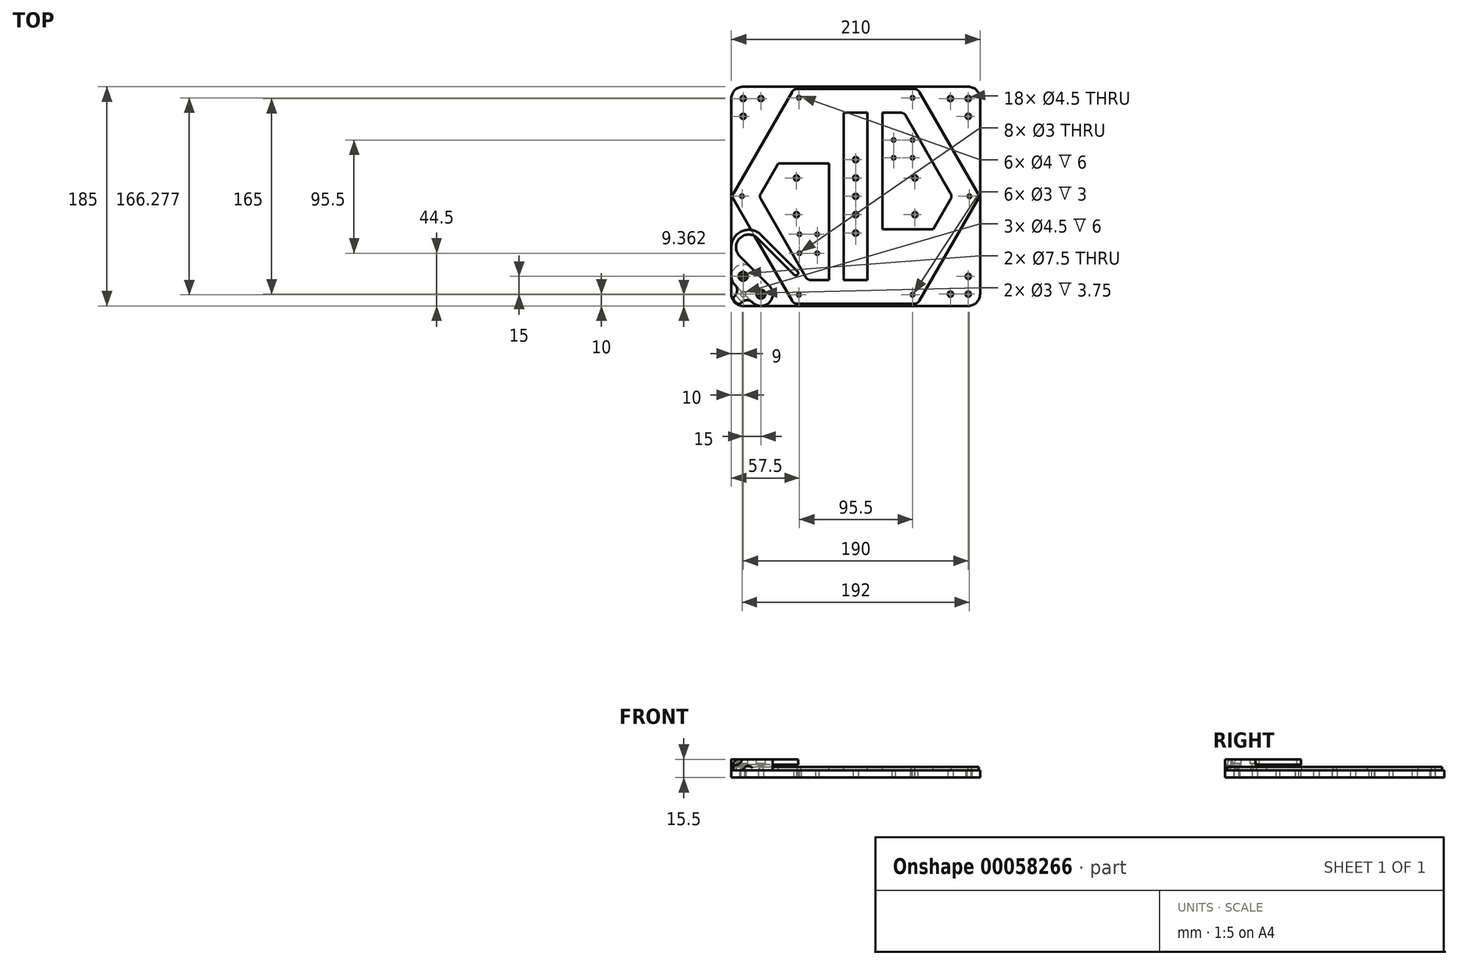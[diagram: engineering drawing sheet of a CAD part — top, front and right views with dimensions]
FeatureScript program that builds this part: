
annotation { "Feature Type Name" : "Feature", "Feature Type Description" : "" }
export const myFeature = defineFeature(function(context is Context, id is Id, definition is map)
    precondition{}
    {
        {
            var Q0;
            Q0=qCreatedBy(makeId("Top.planeOp"),FACE);
            var sketch = newSketch(context, id + "F0", { "sketchPlane" : qUnion([Q0])});
            skLineSegment(sketch, "E0.bottom", {"start": v(105, 92.5) * mm, "end": v(-105, 92.5) * mm});
            skLineSegment(sketch, "E0.top", {"start": v(105, -92.5) * mm, "end": v(-105, -92.5) * mm});
            skLineSegment(sketch, "E0.left", {"start": v(105, 92.5) * mm, "end": v(105, -92.5) * mm});
            skLineSegment(sketch, "E0.right", {"start": v(-105, 92.5) * mm, "end": v(-105, -92.5) * mm});
            skPoint(sketch, "E0.middle", {"position": v(0, 0) * mm});
            skCircle(sketch, "E1", {"center": v(0, 0) * mm, "radius": 96 * mm, "construction": true});
            skLineSegment(sketch, "E2", {"start": v(0, 0) * mm, "end": v(-96, 0) * mm, "construction": true});
            skCircle(sketch, "E3", {"center": v(-96, 0) * mm, "radius": 2 * mm});
            skCircle(sketch, "E4.1.0", {"center": v(-48, -83.14) * mm, "radius": 2 * mm});
            skCircle(sketch, "E4.2.0", {"center": v(48, -83.14) * mm, "radius": 2 * mm});
            skCircle(sketch, "E4.3.0", {"center": v(96, 0) * mm, "radius": 2 * mm});
            skCircle(sketch, "E4.4.0", {"center": v(48, 83.14) * mm, "radius": 2 * mm});
            skCircle(sketch, "E4.5.0", {"center": v(-48, 83.14) * mm, "radius": 2 * mm});
            skSolve(sketch);
        }
        {
            var Q0;
            Q0 = qSketchRegion(id + "F0", true);
            extrude(context, id + "F1", {"entities" : qUnion([Q0]), "depth" : 6 * mm});
        }
        {
            var Q0;
            Q0=makeQuery(id+"F1.opExtrude","SWEPT_EDGE",EDGE,{"disambiguationData":[OSD([sQuery(id+"F0.wireOp",EDGE,"E0.top"),sQuery(id+"F0.wireOp",EDGE,"E0.right")])]});
            var Q1;
            Q1=makeQuery(id+"F1.opExtrude","SWEPT_EDGE",EDGE,{"disambiguationData":[OSD([sQuery(id+"F0.wireOp",EDGE,"E0.top"),sQuery(id+"F0.wireOp",EDGE,"E0.left")])]});
            var Q2;
            Q2=makeQuery(id+"F1.opExtrude","SWEPT_EDGE",EDGE,{"disambiguationData":[OSD([sQuery(id+"F0.wireOp",EDGE,"E0.bottom"),sQuery(id+"F0.wireOp",EDGE,"E0.right")])]});
            var Q3;
            Q3=makeQuery(id+"F1.opExtrude","SWEPT_EDGE",EDGE,{"disambiguationData":[OSD([sQuery(id+"F0.wireOp",EDGE,"E0.bottom"),sQuery(id+"F0.wireOp",EDGE,"E0.left")])]});
            fillet(context, id + "F2", {"entities" : qUnion([Q0, Q1, Q2, Q3]), "radius" : 10 * mm, "tangentPropagation" : true, "allowEdgeOverflow" : false});
        }
        {
            var Q0;
            Q0=makeQuery(id+"F1.opExtrude","CAP_FACE",FACE,{"disambiguationData":[OSD([sQuery(id+"F0.wireOp",EDGE,"E0.bottom"),sQuery(id+"F0.wireOp",EDGE,"E0.top"),sQuery(id+"F0.wireOp",EDGE,"E0.left"),sQuery(id+"F0.wireOp",EDGE,"E0.right"),sQuery(id+"F0.wireOp",EDGE,"E3"),sQuery(id+"F0.wireOp",EDGE,"E4.1.0"),sQuery(id+"F0.wireOp",EDGE,"E4.2.0"),sQuery(id+"F0.wireOp",EDGE,"E4.3.0"),sQuery(id+"F0.wireOp",EDGE,"E4.4.0"),sQuery(id+"F0.wireOp",EDGE,"E4.5.0")])],"isStart":true});
            var sketch = newSketch(context, id + "F3", { "sketchPlane" : qUnion([Q0])});
            skLineSegment(sketch, "E5", {"start": v(0, 0) * mm, "end": v(-105, 0) * mm, "construction": true});
            skCircle(sketch, "E6", {"center": v(0, 0) * mm, "radius": 96 * mm, "construction": true});
            skPoint(sketch, "E7", {"position": v(-96, 0) * mm});
            skLineSegment(sketch, "E8.bottom", {"start": v(40, 40) * mm, "end": v(-40, 40) * mm, "construction": true});
            skLineSegment(sketch, "E8.top", {"start": v(40, -40) * mm, "end": v(-40, -40) * mm, "construction": true});
            skLineSegment(sketch, "E8.left", {"start": v(40, 40) * mm, "end": v(40, -40) * mm, "construction": true});
            skLineSegment(sketch, "E8.right", {"start": v(-40, 40) * mm, "end": v(-40, -40) * mm, "construction": true});
            skLineSegment(sketch, "E9.bottom", {"start": v(-32.5, 48) * mm, "end": v(-47.5, 48) * mm, "construction": true});
            skLineSegment(sketch, "E9.top", {"start": v(-32.5, 32) * mm, "end": v(-47.5, 32) * mm, "construction": true});
            skLineSegment(sketch, "E9.left", {"start": v(-32.5, 48) * mm, "end": v(-32.5, 32) * mm, "construction": true});
            skLineSegment(sketch, "E9.right", {"start": v(-47.5, 48) * mm, "end": v(-47.5, 32) * mm, "construction": true});
            skPoint(sketch, "E9.middle", {"position": v(-40, 40) * mm});
            skCircle(sketch, "E10", {"center": v(-47.5, 48) * mm, "radius": 1.5 * mm});
            skCircle(sketch, "E11", {"center": v(-32.5, 48) * mm, "radius": 1.5 * mm});
            skCircle(sketch, "E12", {"center": v(-47.5, 32) * mm, "radius": 1.5 * mm});
            skCircle(sketch, "E13", {"center": v(-32.5, 32) * mm, "radius": 1.5 * mm});
            skLineSegment(sketch, "E14", {"start": v(0, 0) * mm, "end": v(40, 40) * mm, "construction": true});
            skCircle(sketch, "E15.MirrorC", {"center": v(32, -47.5) * mm, "radius": 1.5 * mm});
            skCircle(sketch, "E16.MirrorC", {"center": v(32, -32.5) * mm, "radius": 1.5 * mm});
            skCircle(sketch, "E17.MirrorC", {"center": v(48, -32.5) * mm, "radius": 1.5 * mm});
            skCircle(sketch, "E18.MirrorC", {"center": v(48, -47.5) * mm, "radius": 1.5 * mm});
            skSolve(sketch);
        }
        {
            var Q0;
            Q0 = qSketchRegion(id + "F3", true);
            extrude(context, id + "F4", {"entities" : qUnion([Q0]), "operationType" : NewBodyOperationType.REMOVE, "endBound" : BoundingType.THROUGH_ALL, "oppositeDirection" : true, "depth" : 25 * mm});
        }
        {
            var Q0;
            Q0=makeQuery(id+"F1.opExtrude","CAP_FACE",FACE,{"disambiguationData":[OSD([sQuery(id+"F0.wireOp",EDGE,"E0.bottom"),sQuery(id+"F0.wireOp",EDGE,"E0.top"),sQuery(id+"F0.wireOp",EDGE,"E0.left"),sQuery(id+"F0.wireOp",EDGE,"E0.right"),sQuery(id+"F0.wireOp",EDGE,"E3"),sQuery(id+"F0.wireOp",EDGE,"E4.1.0"),sQuery(id+"F0.wireOp",EDGE,"E4.2.0"),sQuery(id+"F0.wireOp",EDGE,"E4.3.0"),sQuery(id+"F0.wireOp",EDGE,"E4.4.0"),sQuery(id+"F0.wireOp",EDGE,"E4.5.0")])],"isStart":true});
            var sketch = newSketch(context, id + "F5", { "sketchPlane" : qUnion([Q0])});
            skLineSegment(sketch, "E19", {"start": v(-47.5, 48) * mm, "end": v(-32.5, 32) * mm, "construction": true});
            skLineSegment(sketch, "E20", {"start": v(32, -32.5) * mm, "end": v(48, -47.5) * mm, "construction": true});
            skPoint(sketch, "E21", {"position": v(40, -40) * mm});
            skPoint(sketch, "E22", {"position": v(-40, 40) * mm});
            skLineSegment(sketch, "E23", {"start": v(40, -40) * mm, "end": v(40, -15.5) * mm, "construction": true});
            skLineSegment(sketch, "E24", {"start": v(40, -15.5) * mm, "end": v(0, -15.5) * mm, "construction": true});
            skLineSegment(sketch, "E25", {"start": v(0, -15.5) * mm, "end": v(0, 0) * mm, "construction": true});
            skLineSegment(sketch, "E26.bottom", {"start": v(15.5, 0) * mm, "end": v(-15.5, 0) * mm, "construction": true});
            skLineSegment(sketch, "E26.top", {"start": v(15.5, -31) * mm, "end": v(-15.5, -31) * mm, "construction": true});
            skLineSegment(sketch, "E26.left", {"start": v(15.5, 0) * mm, "end": v(15.5, -31) * mm, "construction": true});
            skLineSegment(sketch, "E26.right", {"start": v(-15.5, 0) * mm, "end": v(-15.5, -31) * mm, "construction": true});
            skPoint(sketch, "E26.middle", {"position": v(0, -15.5) * mm});
            skCircle(sketch, "E27", {"center": v(0, -31) * mm, "radius": 2.25 * mm});
            skCircle(sketch, "E28", {"center": v(0, 0) * mm, "radius": 2.25 * mm});
            skCircle(sketch, "E29.MirrorC", {"center": v(0, 31) * mm, "radius": 2.25 * mm});
            skCircle(sketch, "E30", {"center": v(0, -15.5) * mm, "radius": 2.25 * mm});
            skCircle(sketch, "E31.MirrorC", {"center": v(0, 15.5) * mm, "radius": 2.25 * mm});
            skSolve(sketch);
        }
        {
            var Q0;
            Q0 = qSketchRegion(id + "F5", true);
            extrude(context, id + "F6", {"entities" : qUnion([Q0]), "operationType" : NewBodyOperationType.REMOVE, "endBound" : BoundingType.THROUGH_ALL, "oppositeDirection" : true, "depth" : 25 * mm});
        }
        {
            var Q0;
            Q0=makeQuery(id+"F1.opExtrude","CAP_FACE",FACE,{"disambiguationData":[OSD([sQuery(id+"F0.wireOp",EDGE,"E0.bottom"),sQuery(id+"F0.wireOp",EDGE,"E0.top"),sQuery(id+"F0.wireOp",EDGE,"E0.left"),sQuery(id+"F0.wireOp",EDGE,"E0.right"),sQuery(id+"F0.wireOp",EDGE,"E3"),sQuery(id+"F0.wireOp",EDGE,"E4.1.0"),sQuery(id+"F0.wireOp",EDGE,"E4.2.0"),sQuery(id+"F0.wireOp",EDGE,"E4.3.0"),sQuery(id+"F0.wireOp",EDGE,"E4.4.0"),sQuery(id+"F0.wireOp",EDGE,"E4.5.0")])],"isStart":true});
            var sketch = newSketch(context, id + "F7", { "sketchPlane" : qUnion([Q0])});
            skLineSegment(sketch, "E32", {"start": v(0, 0) * mm, "end": v(49.14, 0) * mm, "construction": true});
            skLineSegment(sketch, "E33", {"start": v(0, 0) * mm, "end": v(0, -73.64) * mm, "construction": true});
            skLineSegment(sketch, "E34", {"start": v(0, 15.5) * mm, "end": v(50, 15.5) * mm, "construction": true});
            skCircle(sketch, "E35", {"center": v(50, 15.5) * mm, "radius": 2.25 * mm});
            skCircle(sketch, "E36.MirrorC", {"center": v(50, -15.5) * mm, "radius": 2.25 * mm});
            skCircle(sketch, "E37.MirrorC", {"center": v(-50, 15.5) * mm, "radius": 2.25 * mm});
            skCircle(sketch, "E38.MirrorC", {"center": v(-50, -15.5) * mm, "radius": 2.25 * mm});
            skSolve(sketch);
        }
        {
            var Q0;
            Q0 = qSketchRegion(id + "F7", true);
            extrude(context, id + "F8", {"entities" : qUnion([Q0]), "operationType" : NewBodyOperationType.REMOVE, "endBound" : BoundingType.THROUGH_ALL, "oppositeDirection" : true, "depth" : 25 * mm});
        }
        {
            var Q0;
            Q0=makeQuery(id+"F1.opExtrude","CAP_FACE",FACE,{"disambiguationData":[OSD([sQuery(id+"F0.wireOp",EDGE,"E0.bottom"),sQuery(id+"F0.wireOp",EDGE,"E0.top"),sQuery(id+"F0.wireOp",EDGE,"E0.left"),sQuery(id+"F0.wireOp",EDGE,"E0.right"),sQuery(id+"F0.wireOp",EDGE,"E3"),sQuery(id+"F0.wireOp",EDGE,"E4.1.0"),sQuery(id+"F0.wireOp",EDGE,"E4.2.0"),sQuery(id+"F0.wireOp",EDGE,"E4.3.0"),sQuery(id+"F0.wireOp",EDGE,"E4.4.0"),sQuery(id+"F0.wireOp",EDGE,"E4.5.0")])],"isStart":true});
            var sketch = newSketch(context, id + "F9", { "sketchPlane" : qUnion([Q0])});
            skCircle(sketch, "E39", {"center": v(0, 0) * mm, "radius": 96 * mm, "construction": true});
            skPoint(sketch, "E40", {"position": v(96, 0) * mm});
            skLineSegment(sketch, "E41", {"start": v(0, 0) * mm, "end": v(95, 82.5) * mm, "construction": true});
            skCircle(sketch, "E42", {"center": v(95, 82.5) * mm, "radius": 2.25 * mm});
            skLineSegment(sketch, "E43", {"start": v(95, 82.5) * mm, "end": v(95, 67.5) * mm, "construction": true});
            skCircle(sketch, "E44", {"center": v(95, 67.5) * mm, "radius": 2.25 * mm});
            skLineSegment(sketch, "E45", {"start": v(95, 82.5) * mm, "end": v(80, 82.5) * mm, "construction": true});
            skCircle(sketch, "E46", {"center": v(80, 82.5) * mm, "radius": 2.25 * mm});
            skLineSegment(sketch, "E47", {"start": v(0, 0) * mm, "end": v(0, 67.43) * mm, "construction": true});
            skLineSegment(sketch, "E48", {"start": v(0, 0) * mm, "end": v(-61.9, 0) * mm, "construction": true});
            skCircle(sketch, "E49.MirrorC", {"center": v(-95, 67.5) * mm, "radius": 2.25 * mm});
            skCircle(sketch, "E50.MirrorC", {"center": v(-95, 82.5) * mm, "radius": 2.25 * mm});
            skCircle(sketch, "E51.MirrorC", {"center": v(-80, 82.5) * mm, "radius": 2.25 * mm});
            skCircle(sketch, "E52.MirrorC", {"center": v(95, -67.5) * mm, "radius": 2.25 * mm});
            skCircle(sketch, "E53.MirrorC", {"center": v(95, -82.5) * mm, "radius": 2.25 * mm});
            skCircle(sketch, "E54.MirrorC", {"center": v(80, -82.5) * mm, "radius": 2.25 * mm});
            skCircle(sketch, "E55.MirrorC", {"center": v(-95, -67.5) * mm, "radius": 2.25 * mm});
            skCircle(sketch, "E56.MirrorC", {"center": v(-95, -82.5) * mm, "radius": 2.25 * mm});
            skCircle(sketch, "E57.MirrorC", {"center": v(-80, -82.5) * mm, "radius": 2.25 * mm});
            skSolve(sketch);
        }
        {
            var Q0;
            Q0 = qSketchRegion(id + "F9", true);
            extrude(context, id + "F10", {"entities" : qUnion([Q0]), "operationType" : NewBodyOperationType.REMOVE, "endBound" : BoundingType.THROUGH_ALL, "oppositeDirection" : true, "depth" : 25 * mm});
        }
        {
            var Q0;
            Q0=makeQuery(id+"F1.opExtrude","CAP_FACE",FACE,{"disambiguationData":[OSD([sQuery(id+"F0.wireOp",EDGE,"E0.bottom"),sQuery(id+"F0.wireOp",EDGE,"E0.top"),sQuery(id+"F0.wireOp",EDGE,"E0.left"),sQuery(id+"F0.wireOp",EDGE,"E0.right"),sQuery(id+"F0.wireOp",EDGE,"E3"),sQuery(id+"F0.wireOp",EDGE,"E4.1.0"),sQuery(id+"F0.wireOp",EDGE,"E4.2.0"),sQuery(id+"F0.wireOp",EDGE,"E4.3.0"),sQuery(id+"F0.wireOp",EDGE,"E4.4.0"),sQuery(id+"F0.wireOp",EDGE,"E4.5.0")])],"isStart":false});
            var sketch = newSketch(context, id + "F11", { "sketchPlane" : qUnion([Q0])});
            skLineSegment(sketch, "E58", {"start": v(-48, 83.14) * mm, "end": v(-96, 0) * mm, "construction": true});
            skLineSegment(sketch, "E59", {"start": v(-96, 0) * mm, "end": v(-48, -83.14) * mm, "construction": true});
            skLineSegment(sketch, "E60", {"start": v(-48, -83.14) * mm, "end": v(48, -83.14) * mm, "construction": true});
            skLineSegment(sketch, "E61", {"start": v(48, -83.14) * mm, "end": v(96, 0) * mm, "construction": true});
            skLineSegment(sketch, "E62", {"start": v(96, 0) * mm, "end": v(48, 83.14) * mm, "construction": true});
            skLineSegment(sketch, "E63", {"start": v(48, 83.14) * mm, "end": v(-48, 83.14) * mm, "construction": true});
            skLineSegment(sketch, "E64.0", {"start": v(104.66, 0) * mm, "end": v(52.33, 90.64) * mm});
            skLineSegment(sketch, "E64.1", {"start": v(-52.33, 90.64) * mm, "end": v(-104.66, 0) * mm});
            skLineSegment(sketch, "E64.2", {"start": v(-104.66, 0) * mm, "end": v(-52.33, -90.64) * mm});
            skLineSegment(sketch, "E64.3", {"start": v(52.33, 90.64) * mm, "end": v(-52.33, 90.64) * mm});
            skLineSegment(sketch, "E64.4", {"start": v(-52.33, -90.64) * mm, "end": v(52.33, -90.64) * mm});
            skLineSegment(sketch, "E64.5", {"start": v(52.33, -90.64) * mm, "end": v(104.66, 0) * mm});
            skLineSegment(sketch, "E65.0", {"start": v(81.57, 0) * mm, "end": v(40.78, 70.64) * mm});
            skLineSegment(sketch, "E65.1", {"start": v(-40.78, 70.64) * mm, "end": v(-81.57, 0) * mm});
            skLineSegment(sketch, "E65.2", {"start": v(-81.57, 0) * mm, "end": v(-40.78, -70.64) * mm});
            skLineSegment(sketch, "E65.3", {"start": v(40.78, 70.64) * mm, "end": v(-40.78, 70.64) * mm});
            skLineSegment(sketch, "E65.4", {"start": v(-40.78, -70.64) * mm, "end": v(40.78, -70.64) * mm});
            skLineSegment(sketch, "E65.5", {"start": v(40.78, -70.64) * mm, "end": v(81.57, 0) * mm});
            skCircle(sketch, "E66", {"center": v(-48, 83.14) * mm, "radius": 1.5 * mm});
            skCircle(sketch, "E67", {"center": v(48, 83.14) * mm, "radius": 1.5 * mm});
            skCircle(sketch, "E68", {"center": v(96, 0) * mm, "radius": 1.5 * mm});
            skCircle(sketch, "E69", {"center": v(48, -83.14) * mm, "radius": 1.5 * mm});
            skCircle(sketch, "E70", {"center": v(-48, -83.14) * mm, "radius": 1.5 * mm});
            skCircle(sketch, "E71", {"center": v(-96, 0) * mm, "radius": 1.5 * mm});
            skSolve(sketch);
        }
        {
            var Q0;
            Q0 = qSketchRegion(id + "F11", true);
            extrude(context, id + "F12", {"entities" : qUnion([Q0]), "depth" : 3 * mm});
        }
        {
            var Q0;
            Q0=makeQuery(id+"F12.opExtrude","CAP_FACE",FACE,{"disambiguationData":[OSD([sQuery(id+"F11.wireOp",EDGE,"E64.0"),sQuery(id+"F11.wireOp",EDGE,"E64.1"),sQuery(id+"F11.wireOp",EDGE,"E64.2"),sQuery(id+"F11.wireOp",EDGE,"E64.3"),sQuery(id+"F11.wireOp",EDGE,"E64.4"),sQuery(id+"F11.wireOp",EDGE,"E64.5"),sQuery(id+"F11.wireOp",EDGE,"E65.0"),sQuery(id+"F11.wireOp",EDGE,"E65.1"),sQuery(id+"F11.wireOp",EDGE,"E65.2"),sQuery(id+"F11.wireOp",EDGE,"E65.3"),sQuery(id+"F11.wireOp",EDGE,"E65.4"),sQuery(id+"F11.wireOp",EDGE,"E65.5"),sQuery(id+"F11.wireOp",EDGE,"E66"),sQuery(id+"F11.wireOp",EDGE,"E67"),sQuery(id+"F11.wireOp",EDGE,"E68"),sQuery(id+"F11.wireOp",EDGE,"E69"),sQuery(id+"F11.wireOp",EDGE,"E70"),sQuery(id+"F11.wireOp",EDGE,"E71")])],"isStart":false});
            var sketch = newSketch(context, id + "F13", { "sketchPlane" : qUnion([Q0])});
            skLineSegment(sketch, "E72", {"start": v(0, 70.64) * mm, "end": v(0, -70.64) * mm, "construction": true});
            skLineSegment(sketch, "E73.bottom", {"start": v(-10, 70.64) * mm, "end": v(-22.5, 70.64) * mm});
            skLineSegment(sketch, "E73.top", {"start": v(-10, -70.64) * mm, "end": v(-22.5, -70.64) * mm});
            skLineSegment(sketch, "E73.left", {"start": v(-10, 70.64) * mm, "end": v(-10, -70.64) * mm});
            skLineSegment(sketch, "E73.right", {"start": v(-22.5, 70.64) * mm, "end": v(-22.5, -70.64) * mm});
            skLineSegment(sketch, "E74.MirrorCS", {"start": v(22.5, 70.64) * mm, "end": v(22.5, -70.64) * mm});
            skLineSegment(sketch, "E75.MirrorCS", {"start": v(10, -70.64) * mm, "end": v(22.5, -70.64) * mm});
            skLineSegment(sketch, "E76.MirrorCS", {"start": v(10, 70.64) * mm, "end": v(10, -70.64) * mm});
            skLineSegment(sketch, "E77.MirrorCS", {"start": v(10, 70.64) * mm, "end": v(22.5, 70.64) * mm});
            skSolve(sketch);
        }
        {
            var Q0;
            Q0 = qSketchRegion(id + "F13", true);
            var Q1;
            Q1=makeQuery(id+"F12.opExtrude","CAP_FACE",FACE,{"disambiguationData":[OSD([sQuery(id+"F11.wireOp",EDGE,"E64.0"),sQuery(id+"F11.wireOp",EDGE,"E64.1"),sQuery(id+"F11.wireOp",EDGE,"E64.2"),sQuery(id+"F11.wireOp",EDGE,"E64.3"),sQuery(id+"F11.wireOp",EDGE,"E64.4"),sQuery(id+"F11.wireOp",EDGE,"E64.5"),sQuery(id+"F11.wireOp",EDGE,"E65.0"),sQuery(id+"F11.wireOp",EDGE,"E65.1"),sQuery(id+"F11.wireOp",EDGE,"E65.2"),sQuery(id+"F11.wireOp",EDGE,"E65.3"),sQuery(id+"F11.wireOp",EDGE,"E65.4"),sQuery(id+"F11.wireOp",EDGE,"E65.5"),sQuery(id+"F11.wireOp",EDGE,"E66"),sQuery(id+"F11.wireOp",EDGE,"E67"),sQuery(id+"F11.wireOp",EDGE,"E68"),sQuery(id+"F11.wireOp",EDGE,"E69"),sQuery(id+"F11.wireOp",EDGE,"E70"),sQuery(id+"F11.wireOp",EDGE,"E71")])],"isStart":true});
            extrude(context, id + "F14", {"entities" : qUnion([Q0]), "operationType" : NewBodyOperationType.ADD, "endBound" : BoundingType.UP_TO_SURFACE, "oppositeDirection" : true, "endBoundEntityFace" : qUnion([Q1]), "depth" : 25 * mm});
        }
        {
            var Q0;
            Q0=makeQuery(id+"F14.boolean.opBoolean","MERGE",FACE,{"derivedFrom":[makeQuery(id+"F12.opExtrude","CAP_FACE",FACE,{"disambiguationData":[OSD([sQuery(id+"F11.wireOp",EDGE,"E64.0"),sQuery(id+"F11.wireOp",EDGE,"E64.1"),sQuery(id+"F11.wireOp",EDGE,"E64.2"),sQuery(id+"F11.wireOp",EDGE,"E64.3"),sQuery(id+"F11.wireOp",EDGE,"E64.4"),sQuery(id+"F11.wireOp",EDGE,"E64.5"),sQuery(id+"F11.wireOp",EDGE,"E65.0"),sQuery(id+"F11.wireOp",EDGE,"E65.1"),sQuery(id+"F11.wireOp",EDGE,"E65.2"),sQuery(id+"F11.wireOp",EDGE,"E65.3"),sQuery(id+"F11.wireOp",EDGE,"E65.4"),sQuery(id+"F11.wireOp",EDGE,"E65.5"),sQuery(id+"F11.wireOp",EDGE,"E66"),sQuery(id+"F11.wireOp",EDGE,"E67"),sQuery(id+"F11.wireOp",EDGE,"E68"),sQuery(id+"F11.wireOp",EDGE,"E69"),sQuery(id+"F11.wireOp",EDGE,"E70"),sQuery(id+"F11.wireOp",EDGE,"E71")])],"isStart":false}),makeQuery(id+"F14.opExtrude","CAP_FACE",FACE,{"disambiguationData":[OSD([sQuery(id+"F13.wireOp",EDGE,"E73.bottom"),sQuery(id+"F13.wireOp",EDGE,"E73.top"),sQuery(id+"F13.wireOp",EDGE,"E73.left"),sQuery(id+"F13.wireOp",EDGE,"E73.right")])],"isStart":true}),makeQuery(id+"F14.opExtrude","CAP_FACE",FACE,{"disambiguationData":[OSD([sQuery(id+"F13.wireOp",EDGE,"E74.MirrorCS"),sQuery(id+"F13.wireOp",EDGE,"E75.MirrorCS"),sQuery(id+"F13.wireOp",EDGE,"E76.MirrorCS"),sQuery(id+"F13.wireOp",EDGE,"E77.MirrorCS")])],"isStart":true})]});
            var sketch = newSketch(context, id + "F15", { "sketchPlane" : qUnion([Q0])});
            skLineSegment(sketch, "E78", {"start": v(-40.78, 70.64) * mm, "end": v(-22.5, 70.64) * mm});
            skLineSegment(sketch, "E79", {"start": v(-22.5, 70.64) * mm, "end": v(-22.5, 27.75) * mm});
            skLineSegment(sketch, "E80", {"start": v(-22.5, 27.75) * mm, "end": v(-65.54, 27.75) * mm});
            skLineSegment(sketch, "E81", {"start": v(-65.54, 27.75) * mm, "end": v(-40.78, 70.64) * mm});
            skLineSegment(sketch, "E82", {"start": v(22.5, -70.64) * mm, "end": v(40.78, -70.64) * mm});
            skLineSegment(sketch, "E83", {"start": v(40.78, -70.64) * mm, "end": v(65.54, -27.75) * mm});
            skLineSegment(sketch, "E84", {"start": v(65.54, -27.75) * mm, "end": v(22.5, -27.75) * mm});
            skLineSegment(sketch, "E85", {"start": v(22.5, -27.75) * mm, "end": v(22.5, -70.64) * mm});
            skSolve(sketch);
        }
        {
            var Q0;
            Q0 = qSketchRegion(id + "F15", true);
            var Q1;
            {var subQ0=sQuery(id+"F11.wireOp",EDGE,"E71");var subQ1=sQuery(id+"F11.wireOp",EDGE,"E70");var subQ2=sQuery(id+"F11.wireOp",EDGE,"E69");var subQ3=sQuery(id+"F11.wireOp",EDGE,"E68");var subQ4=sQuery(id+"F11.wireOp",EDGE,"E67");var subQ5=sQuery(id+"F11.wireOp",EDGE,"E66");var subQ6=sQuery(id+"F11.wireOp",EDGE,"E65.5");var subQ7=sQuery(id+"F11.wireOp",EDGE,"E65.4");var subQ8=sQuery(id+"F11.wireOp",EDGE,"E65.3");var subQ9=sQuery(id+"F11.wireOp",EDGE,"E65.2");var subQ10=sQuery(id+"F11.wireOp",EDGE,"E65.1");var subQ11=sQuery(id+"F11.wireOp",EDGE,"E65.0");var subQ12=sQuery(id+"F11.wireOp",EDGE,"E64.5");var subQ13=sQuery(id+"F11.wireOp",EDGE,"E64.4");var subQ14=sQuery(id+"F11.wireOp",EDGE,"E64.3");var subQ15=sQuery(id+"F11.wireOp",EDGE,"E64.2");var subQ16=sQuery(id+"F11.wireOp",EDGE,"E64.1");var subQ17=sQuery(id+"F11.wireOp",EDGE,"E64.0");Q1=makeQuery(id+"F14.boolean.opBoolean","MERGE",FACE,{"derivedFrom":[makeQuery(id+"F12.opExtrude","CAP_FACE",FACE,{"disambiguationData":[OSD([subQ17,subQ16,subQ15,subQ14,subQ13,subQ12,subQ11,subQ10,subQ9,subQ8,subQ7,subQ6,subQ5,subQ4,subQ3,subQ2,subQ1,subQ0])],"isStart":true}),makeQuery(id+"F14.opExtrude","CAP_FACE",FACE,{"disambiguationData":[OSD([subQ17,subQ16,subQ15,subQ14,subQ13,subQ12,subQ11,subQ10,subQ9,subQ8,subQ7,subQ6,subQ5,subQ4,subQ3,subQ2,subQ1,subQ0]),ownerDisambiguation([makeQuery(id+"F13.imprint","IMPRINT",EDGE,{"derivedFrom":sQuery(id+"F13.wireOp",EDGE,"E73.bottom")})])],"isStart":false}),makeQuery(id+"F14.opExtrude","CAP_FACE",FACE,{"disambiguationData":[OSD([subQ17,subQ16,subQ15,subQ14,subQ13,subQ12,subQ11,subQ10,subQ9,subQ8,subQ7,subQ6,subQ5,subQ4,subQ3,subQ2,subQ1,subQ0]),ownerDisambiguation([makeQuery(id+"F13.imprint","IMPRINT",EDGE,{"derivedFrom":sQuery(id+"F13.wireOp",EDGE,"E74.MirrorCS")})])],"isStart":false})]});}
            extrude(context, id + "F16", {"entities" : qUnion([Q0]), "operationType" : NewBodyOperationType.ADD, "endBound" : BoundingType.UP_TO_SURFACE, "oppositeDirection" : true, "endBoundEntityFace" : qUnion([Q1]), "depth" : 25 * mm});
        }
        {
            var Q0;
            Q0=makeQuery(id+"F12.opExtrude","SWEPT_EDGE",EDGE,{"disambiguationData":[OSD([sQuery(id+"F11.wireOp",EDGE,"E64.1"),sQuery(id+"F11.wireOp",EDGE,"E64.3")])]});
            var Q1;
            Q1=makeQuery(id+"F12.opExtrude","SWEPT_EDGE",EDGE,{"disambiguationData":[OSD([sQuery(id+"F11.wireOp",EDGE,"E64.1"),sQuery(id+"F11.wireOp",EDGE,"E64.2")])]});
            var Q2;
            Q2=makeQuery(id+"F12.opExtrude","SWEPT_EDGE",EDGE,{"disambiguationData":[OSD([sQuery(id+"F11.wireOp",EDGE,"E64.2"),sQuery(id+"F11.wireOp",EDGE,"E64.4")])]});
            var Q3;
            Q3=makeQuery(id+"F12.opExtrude","SWEPT_EDGE",EDGE,{"disambiguationData":[OSD([sQuery(id+"F11.wireOp",EDGE,"E64.4"),sQuery(id+"F11.wireOp",EDGE,"E64.5")])]});
            var Q4;
            Q4=makeQuery(id+"F12.opExtrude","SWEPT_EDGE",EDGE,{"disambiguationData":[OSD([sQuery(id+"F11.wireOp",EDGE,"E64.0"),sQuery(id+"F11.wireOp",EDGE,"E64.5")])]});
            var Q5;
            Q5=makeQuery(id+"F12.opExtrude","SWEPT_EDGE",EDGE,{"disambiguationData":[OSD([sQuery(id+"F11.wireOp",EDGE,"E64.0"),sQuery(id+"F11.wireOp",EDGE,"E64.3")])]});
            var Q6;
            Q6=makeQuery(id+"F12.opExtrude","SWEPT_EDGE",EDGE,{"disambiguationData":[OSD([sQuery(id+"F11.wireOp",EDGE,"E65.1"),sQuery(id+"F11.wireOp",EDGE,"E65.2")])]});
            var Q7;
            Q7=makeQuery(id+"F12.opExtrude","SWEPT_EDGE",EDGE,{"disambiguationData":[OSD([sQuery(id+"F11.wireOp",EDGE,"E65.2"),sQuery(id+"F11.wireOp",EDGE,"E65.4")])]});
            var Q8;
            Q8=makeQuery(id+"F14.opExtrude","SWEPT_EDGE",EDGE,{"disambiguationData":[OSD([sQuery(id+"F11.wireOp",EDGE,"E65.4"),sQuery(id+"F13.wireOp",EDGE,"E73.top"),sQuery(id+"F13.wireOp",EDGE,"E73.right")])]});
            var Q9;
            Q9=makeQuery(id+"F16.opExtrude","SWEPT_EDGE",EDGE,{"disambiguationData":[OSD([sQuery(id+"F11.wireOp",EDGE,"E65.1"),sQuery(id+"F15.wireOp",EDGE,"E80"),sQuery(id+"F15.wireOp",EDGE,"E81")])]});
            var Q10;
            Q10=makeQuery(id+"F16.opExtrude","SWEPT_EDGE",EDGE,{"disambiguationData":[OSD([sQuery(id+"F13.wireOp",EDGE,"E73.right"),sQuery(id+"F15.wireOp",EDGE,"E79"),sQuery(id+"F15.wireOp",EDGE,"E80")])]});
            var Q11;
            Q11=makeQuery(id+"F14.opExtrude","SWEPT_EDGE",EDGE,{"disambiguationData":[OSD([sQuery(id+"F11.wireOp",EDGE,"E65.3"),sQuery(id+"F13.wireOp",EDGE,"E73.bottom"),sQuery(id+"F13.wireOp",EDGE,"E73.left")])]});
            var Q12;
            Q12=makeQuery(id+"F14.opExtrude","SWEPT_EDGE",EDGE,{"disambiguationData":[OSD([sQuery(id+"F11.wireOp",EDGE,"E65.3"),sQuery(id+"F13.wireOp",EDGE,"E76.MirrorCS"),sQuery(id+"F13.wireOp",EDGE,"E77.MirrorCS")])]});
            var Q13;
            Q13=makeQuery(id+"F14.opExtrude","SWEPT_EDGE",EDGE,{"disambiguationData":[OSD([sQuery(id+"F11.wireOp",EDGE,"E65.4"),sQuery(id+"F13.wireOp",EDGE,"E75.MirrorCS"),sQuery(id+"F13.wireOp",EDGE,"E76.MirrorCS")])]});
            var Q14;
            Q14=makeQuery(id+"F14.opExtrude","SWEPT_EDGE",EDGE,{"disambiguationData":[OSD([sQuery(id+"F11.wireOp",EDGE,"E65.4"),sQuery(id+"F13.wireOp",EDGE,"E73.top"),sQuery(id+"F13.wireOp",EDGE,"E73.left")])]});
            var Q15;
            Q15=makeQuery(id+"F16.opExtrude","SWEPT_EDGE",EDGE,{"disambiguationData":[OSD([sQuery(id+"F13.wireOp",EDGE,"E74.MirrorCS"),sQuery(id+"F15.wireOp",EDGE,"E84"),sQuery(id+"F15.wireOp",EDGE,"E85")])]});
            var Q16;
            Q16=makeQuery(id+"F16.opExtrude","SWEPT_EDGE",EDGE,{"disambiguationData":[OSD([sQuery(id+"F11.wireOp",EDGE,"E65.5"),sQuery(id+"F15.wireOp",EDGE,"E83"),sQuery(id+"F15.wireOp",EDGE,"E84")])]});
            var Q17;
            Q17=makeQuery(id+"F12.opExtrude","SWEPT_EDGE",EDGE,{"disambiguationData":[OSD([sQuery(id+"F11.wireOp",EDGE,"E65.0"),sQuery(id+"F11.wireOp",EDGE,"E65.5")])]});
            var Q18;
            Q18=makeQuery(id+"F12.opExtrude","SWEPT_EDGE",EDGE,{"disambiguationData":[OSD([sQuery(id+"F11.wireOp",EDGE,"E65.0"),sQuery(id+"F11.wireOp",EDGE,"E65.3")])]});
            var Q19;
            Q19=makeQuery(id+"F14.opExtrude","SWEPT_EDGE",EDGE,{"disambiguationData":[OSD([sQuery(id+"F11.wireOp",EDGE,"E65.3"),sQuery(id+"F13.wireOp",EDGE,"E74.MirrorCS"),sQuery(id+"F13.wireOp",EDGE,"E77.MirrorCS")])]});
            fillet(context, id + "F17", {"entities" : qUnion([Q0, Q1, Q2, Q3, Q4, Q5, Q6, Q7, Q8, Q9, Q10, Q11, Q12, Q13, Q14, Q15, Q16, Q17, Q18, Q19]), "radius" : 5 * mm, "tangentPropagation" : true, "allowEdgeOverflow" : false});
        }
        {
            var Q0;
            Q0=makeQuery(id+"F1.opExtrude","CAP_FACE",FACE,{"disambiguationData":[OSD([sQuery(id+"F0.wireOp",EDGE,"E0.bottom"),sQuery(id+"F0.wireOp",EDGE,"E0.top"),sQuery(id+"F0.wireOp",EDGE,"E0.left"),sQuery(id+"F0.wireOp",EDGE,"E0.right"),sQuery(id+"F0.wireOp",EDGE,"E3"),sQuery(id+"F0.wireOp",EDGE,"E4.1.0"),sQuery(id+"F0.wireOp",EDGE,"E4.2.0"),sQuery(id+"F0.wireOp",EDGE,"E4.3.0"),sQuery(id+"F0.wireOp",EDGE,"E4.4.0"),sQuery(id+"F0.wireOp",EDGE,"E4.5.0")])],"isStart":false});
            var sketch = newSketch(context, id + "F18", { "sketchPlane" : qUnion([Q0])});
            skCircle(sketch, "E86", {"center": v(0, 0) * mm, "radius": 90 * mm, "construction": true});
            skArc(sketch, "E87.0", {"start": v(-105, -82.5) * mm, "mid": v(-102.07, -89.57) * mm, "end": v(-95, -92.5) * mm});
            skLineSegment(sketch, "E88", {"start": v(-105, -82.5) * mm, "end": v(-105, -67.5) * mm});
            skLineSegment(sketch, "E89", {"start": v(-95, -92.5) * mm, "end": v(-80, -92.5) * mm});
            skArc(sketch, "E90", {"start": v(-87.93, -60.43) * mm, "mid": v(-98.83, -58.26) * mm, "end": v(-105, -67.5) * mm});
            skArc(sketch, "E91", {"start": v(-80, -92.5) * mm, "mid": v(-70.76, -86.33) * mm, "end": v(-72.93, -75.43) * mm});
            skLineSegment(sketch, "E92", {"start": v(-87.93, -60.43) * mm, "end": v(-72.93, -75.43) * mm});
            skCircle(sketch, "E93", {"center": v(-95, -67.5) * mm, "radius": 1.5 * mm});
            skCircle(sketch, "E94", {"center": v(-95, -82.5) * mm, "radius": 1.5 * mm});
            skCircle(sketch, "E95", {"center": v(-80, -82.5) * mm, "radius": 1.5 * mm});
            skSolve(sketch);
        }
        {
            var Q0;
            Q0 = qSketchRegion(id + "F18", true);
            extrude(context, id + "F19", {"entities" : qUnion([Q0]), "depth" : 5 * mm});
        }
        {
            var Q0;
            Q0=makeQuery(id+"F19.opExtrude","CAP_FACE",FACE,{"disambiguationData":[OSD([sQuery(id+"F18.wireOp",EDGE,"E87.0"),sQuery(id+"F18.wireOp",EDGE,"E88"),sQuery(id+"F18.wireOp",EDGE,"E89"),sQuery(id+"F18.wireOp",EDGE,"E90"),sQuery(id+"F18.wireOp",EDGE,"E91"),sQuery(id+"F18.wireOp",EDGE,"E92"),sQuery(id+"F18.wireOp",EDGE,"E93"),sQuery(id+"F18.wireOp",EDGE,"E94"),sQuery(id+"F18.wireOp",EDGE,"E95")])],"isStart":false});
            var sketch = newSketch(context, id + "F20", { "sketchPlane" : qUnion([Q0])});
            skCircle(sketch, "E96", {"center": v(0, 0) * mm, "radius": 84 * mm, "construction": true});
            skLineSegment(sketch, "E97", {"start": v(0, 0) * mm, "end": v(-84, 0) * mm, "construction": true});
            skLineSegment(sketch, "E98", {"start": v(-84, 0) * mm, "end": v(0, -84) * mm, "construction": true});
            skLineSegment(sketch, "E99", {"start": v(-42, -42) * mm, "end": v(-59.4, -59.4) * mm, "construction": true});
            skLineSegment(sketch, "E100.0", {"start": v(-87.93, -60.43) * mm, "end": v(-72.93, -75.43) * mm});
            skLineSegment(sketch, "E100.1", {"start": v(-105, -67.5) * mm, "end": v(-105, -82.5) * mm});
            skArc(sketch, "E100.2", {"start": v(-105, -82.5) * mm, "mid": v(-102.07, -89.57) * mm, "end": v(-95, -92.5) * mm});
            skLineSegment(sketch, "E100.3", {"start": v(-80, -92.5) * mm, "end": v(-95, -92.5) * mm});
            skArc(sketch, "E100.4", {"start": v(-80, -92.5) * mm, "mid": v(-70.76, -86.33) * mm, "end": v(-72.93, -75.43) * mm});
            skCircle(sketch, "E101.0", {"center": v(-95, -67.5) * mm, "radius": 1.5 * mm});
            skCircle(sketch, "E101.1", {"center": v(-95, -82.5) * mm, "radius": 1.5 * mm});
            skCircle(sketch, "E101.2", {"center": v(-80, -82.5) * mm, "radius": 1.5 * mm});
            skLineSegment(sketch, "E102", {"start": v(-49.14, -63.29) * mm, "end": v(-79.9, -32.53) * mm});
            skLineSegment(sketch, "E103", {"start": v(-87.93, -60.43) * mm, "end": v(-97.87, -50.5) * mm});
            skLineSegment(sketch, "E104", {"start": v(-82.73, -35.36) * mm, "end": v(-51.97, -66.11) * mm});
            skArc(sketch, "E105", {"start": v(-51.97, -66.11) * mm, "mid": v(-49.14, -66.11) * mm, "end": v(-49.14, -63.29) * mm});
            skArc(sketch, "E106", {"start": v(-82.73, -35.36) * mm, "mid": v(-97.87, -35.36) * mm, "end": v(-97.87, -50.5) * mm});
            skLineSegment(sketch, "E107", {"start": v(-90.3, -42.92) * mm, "end": v(-101, -42.92) * mm, "construction": true});
            skLineSegment(sketch, "E108", {"start": v(-101, -42.92) * mm, "end": v(-105, -42.92) * mm, "construction": true});
            skLineSegment(sketch, "E109", {"start": v(-82.73, -35.36) * mm, "end": v(-79.9, -32.53) * mm, "construction": true});
            skArc(sketch, "E110", {"start": v(-79.9, -32.53) * mm, "mid": v(-95.92, -29.34) * mm, "end": v(-105, -42.92) * mm});
            skLineSegment(sketch, "E111", {"start": v(-105, -42.92) * mm, "end": v(-105, -67.5) * mm});
            skSolve(sketch);
        }
        {
            var Q0;
            Q0 = qSketchRegion(id + "F20", true);
            extrude(context, id + "F21", {"entities" : qUnion([Q0]), "operationType" : NewBodyOperationType.ADD, "depth" : 4.5 * mm});
        }
        {
            var Q0;
            Q0=makeQuery(id+"F21.opExtrude","CAP_FACE",FACE,{"disambiguationData":[OSD([sQuery(id+"F20.wireOp",EDGE,"E100.0"),sQuery(id+"F20.wireOp",EDGE,"E100.1"),sQuery(id+"F20.wireOp",EDGE,"E100.2"),sQuery(id+"F20.wireOp",EDGE,"E100.3"),sQuery(id+"F20.wireOp",EDGE,"E100.4"),sQuery(id+"F20.wireOp",EDGE,"E101.0"),sQuery(id+"F20.wireOp",EDGE,"E101.1"),sQuery(id+"F20.wireOp",EDGE,"E101.2"),sQuery(id+"F20.wireOp",EDGE,"E102"),sQuery(id+"F20.wireOp",EDGE,"E103"),sQuery(id+"F20.wireOp",EDGE,"E104"),sQuery(id+"F20.wireOp",EDGE,"E105"),sQuery(id+"F20.wireOp",EDGE,"E106"),sQuery(id+"F20.wireOp",EDGE,"E110"),sQuery(id+"F20.wireOp",EDGE,"E111")])],"isStart":false});
            var sketch = newSketch(context, id + "F22", { "sketchPlane" : qUnion([Q0])});
            skCircle(sketch, "E112", {"center": v(-95, -67.5) * mm, "radius": 3.75 * mm});
            skCircle(sketch, "E113", {"center": v(-95, -82.5) * mm, "radius": 3.75 * mm, "construction": true});
            skCircle(sketch, "E114", {"center": v(-80, -82.5) * mm, "radius": 3.75 * mm});
            skSolve(sketch);
        }
        {
            var Q0;
            Q0 = qSketchRegion(id + "F22", true);
            extrude(context, id + "F23", {"entities" : qUnion([Q0]), "operationType" : NewBodyOperationType.REMOVE, "oppositeDirection" : true, "depth" : 3.5 * mm});
        }
        {
            var Q0;
            Q0=makeQuery(id+"F23.boolean.opBoolean","INTERSECT",EDGE,{"derivedFrom":[makeQuery(id+"F21.boolean.opBoolean","MERGE",FACE,{"derivedFrom":[makeQuery(id+"F19.opExtrude","SWEPT_FACE",FACE,{"disambiguationData":[OSD([sQuery(id+"F18.wireOp",EDGE,"E93")])]}),makeQuery(id+"F21.opExtrude","SWEPT_FACE",FACE,{"disambiguationData":[OSD([sQuery(id+"F20.wireOp",EDGE,"E101.0")])]})]}),makeQuery(id+"F23.opExtrude","CAP_FACE",FACE,{"disambiguationData":[OSD([sQuery(id+"F22.wireOp",EDGE,"E112")])],"isStart":false})]});
            var Q1;
            Q1=makeQuery(id+"F23.boolean.opBoolean","INTERSECT",EDGE,{"derivedFrom":[makeQuery(id+"F21.boolean.opBoolean","MERGE",FACE,{"derivedFrom":[makeQuery(id+"F19.opExtrude","SWEPT_FACE",FACE,{"disambiguationData":[OSD([sQuery(id+"F18.wireOp",EDGE,"E95")])]}),makeQuery(id+"F21.opExtrude","SWEPT_FACE",FACE,{"disambiguationData":[OSD([sQuery(id+"F20.wireOp",EDGE,"E101.2")])]})]}),makeQuery(id+"F23.opExtrude","CAP_FACE",FACE,{"disambiguationData":[OSD([sQuery(id+"F22.wireOp",EDGE,"E114")])],"isStart":false})]});
            chamfer(context, id + "F24", {"entities" : qUnion([Q0, Q1]), "width" : 2.25 * mm, "tangentPropagation" : true});
        }
        {
            var Q0;
            Q0=makeQuery(id+"F21.opExtrude","CAP_FACE",FACE,{"disambiguationData":[OSD([sQuery(id+"F20.wireOp",EDGE,"E100.0"),sQuery(id+"F20.wireOp",EDGE,"E100.1"),sQuery(id+"F20.wireOp",EDGE,"E100.2"),sQuery(id+"F20.wireOp",EDGE,"E100.3"),sQuery(id+"F20.wireOp",EDGE,"E100.4"),sQuery(id+"F20.wireOp",EDGE,"E101.0"),sQuery(id+"F20.wireOp",EDGE,"E101.1"),sQuery(id+"F20.wireOp",EDGE,"E101.2"),sQuery(id+"F20.wireOp",EDGE,"E102"),sQuery(id+"F20.wireOp",EDGE,"E103"),sQuery(id+"F20.wireOp",EDGE,"E104"),sQuery(id+"F20.wireOp",EDGE,"E105"),sQuery(id+"F20.wireOp",EDGE,"E106"),sQuery(id+"F20.wireOp",EDGE,"E110"),sQuery(id+"F20.wireOp",EDGE,"E111")])],"isStart":false});
            var sketch = newSketch(context, id + "F25", { "sketchPlane" : qUnion([Q0])});
            skArc(sketch, "E115", {"start": v(-105, -67.5) * mm, "mid": v(-104.24, -71.33) * mm, "end": v(-102.07, -74.57) * mm});
            skArc(sketch, "E116", {"start": v(-80, -92.5) * mm, "mid": v(-83.83, -91.74) * mm, "end": v(-87.07, -89.57) * mm});
            skLineSegment(sketch, "E117", {"start": v(-102.07, -74.57) * mm, "end": v(-87.07, -89.57) * mm});
            skLineSegment(sketch, "E118.0", {"start": v(-105, -67.5) * mm, "end": v(-105, -82.5) * mm});
            skArc(sketch, "E118.1", {"start": v(-105, -82.5) * mm, "mid": v(-102.07, -89.57) * mm, "end": v(-95, -92.5) * mm});
            skLineSegment(sketch, "E118.2", {"start": v(-80, -92.5) * mm, "end": v(-95, -92.5) * mm});
            skPoint(sketch, "E119.orphan", {"position": v(-105, -42.92) * mm});
            skSolve(sketch);
        }
        {
            var Q0;
            Q0 = qSketchRegion(id + "F25", true);
            var Q1;
            Q1=makeQuery(id+"F19.opExtrude","CAP_FACE",FACE,{"disambiguationData":[OSD([sQuery(id+"F18.wireOp",EDGE,"E87.0"),sQuery(id+"F18.wireOp",EDGE,"E88"),sQuery(id+"F18.wireOp",EDGE,"E89"),sQuery(id+"F18.wireOp",EDGE,"E90"),sQuery(id+"F18.wireOp",EDGE,"E91"),sQuery(id+"F18.wireOp",EDGE,"E92"),sQuery(id+"F18.wireOp",EDGE,"E93"),sQuery(id+"F18.wireOp",EDGE,"E94"),sQuery(id+"F18.wireOp",EDGE,"E95")])],"isStart":true});
            extrude(context, id + "F26", {"entities" : qUnion([Q0]), "operationType" : NewBodyOperationType.REMOVE, "endBound" : BoundingType.UP_TO_SURFACE, "oppositeDirection" : true, "endBoundEntityFace" : qUnion([Q1]), "depth" : 25 * mm});
        }
        {
            var Q0;
            Q0=makeQuery(id+"F21.opExtrude","CAP_FACE",FACE,{"disambiguationData":[OSD([sQuery(id+"F20.wireOp",EDGE,"E100.0"),sQuery(id+"F20.wireOp",EDGE,"E100.1"),sQuery(id+"F20.wireOp",EDGE,"E100.2"),sQuery(id+"F20.wireOp",EDGE,"E100.3"),sQuery(id+"F20.wireOp",EDGE,"E100.4"),sQuery(id+"F20.wireOp",EDGE,"E101.0"),sQuery(id+"F20.wireOp",EDGE,"E101.1"),sQuery(id+"F20.wireOp",EDGE,"E101.2"),sQuery(id+"F20.wireOp",EDGE,"E102"),sQuery(id+"F20.wireOp",EDGE,"E103"),sQuery(id+"F20.wireOp",EDGE,"E104"),sQuery(id+"F20.wireOp",EDGE,"E105"),sQuery(id+"F20.wireOp",EDGE,"E106"),sQuery(id+"F20.wireOp",EDGE,"E110"),sQuery(id+"F20.wireOp",EDGE,"E111")])],"isStart":false});
            var sketch = newSketch(context, id + "F27", { "sketchPlane" : qUnion([Q0])});
            skLineSegment(sketch, "E120", {"start": v(-95.54, -81.1) * mm, "end": v(-93.6, -83.04) * mm, "construction": true});
            skLineSegment(sketch, "E121", {"start": v(-95.28, -77.12) * mm, "end": v(-104.47, -86.31) * mm});
            skLineSegment(sketch, "E122", {"start": v(-104.47, -86.31) * mm, "end": v(-98.81, -91.97) * mm});
            skLineSegment(sketch, "E123", {"start": v(-98.81, -91.97) * mm, "end": v(-89.62, -82.78) * mm});
            skLineSegment(sketch, "E124", {"start": v(-89.62, -82.78) * mm, "end": v(-95.28, -77.12) * mm});
            skLineSegment(sketch, "E125", {"start": v(-94.57, -82.07) * mm, "end": v(-92.45, -79.95) * mm, "construction": true});
            skSolve(sketch);
        }
        {
            var Q0;
            Q0 = qSketchRegion(id + "F27", true);
            var Q1;
            Q1=makeQuery(id+"F19.opExtrude","CAP_FACE",FACE,{"disambiguationData":[OSD([sQuery(id+"F18.wireOp",EDGE,"E87.0"),sQuery(id+"F18.wireOp",EDGE,"E88"),sQuery(id+"F18.wireOp",EDGE,"E89"),sQuery(id+"F18.wireOp",EDGE,"E90"),sQuery(id+"F18.wireOp",EDGE,"E91"),sQuery(id+"F18.wireOp",EDGE,"E92"),sQuery(id+"F18.wireOp",EDGE,"E93"),sQuery(id+"F18.wireOp",EDGE,"E94"),sQuery(id+"F18.wireOp",EDGE,"E95")])],"isStart":true});
            extrude(context, id + "F28", {"entities" : qUnion([Q0]), "operationType" : NewBodyOperationType.ADD, "endBound" : BoundingType.UP_TO_SURFACE, "oppositeDirection" : true, "endBoundEntityFace" : qUnion([Q1]), "depth" : 25 * mm});
        }
        {
            var Q0;
            Q0=makeQuery(id+"F28.opExtrude","CAP_EDGE",EDGE,{"disambiguationData":[OSD([sQuery(id+"F27.wireOp",EDGE,"E122")])],"isStart":true});
            chamfer(context, id + "F29", {"entities" : qUnion([Q0]), "width" : 5 * mm, "tangentPropagation" : true});
        }
        {
            var Q0;
            Q0=makeQuery(id+"F28.opExtrude","SWEPT_FACE",FACE,{"disambiguationData":[OSD([sQuery(id+"F27.wireOp",EDGE,"E123")])]});
            var sketch = newSketch(context, id + "F30", { "sketchPlane" : qUnion([Q0])});
            skLineSegment(sketch, "E126", {"start": v(-124.9, 12) * mm, "end": v(-130.9, 6) * mm});
            skLineSegment(sketch, "E127", {"start": v(-130.9, 6) * mm, "end": v(-124.9, 6) * mm});
            skLineSegment(sketch, "E128", {"start": v(-124.9, 6) * mm, "end": v(-124.9, 12) * mm});
            skSolve(sketch);
        }
        {
            var Q0;
            Q0 = qSketchRegion(id + "F30", true);
            var Q1;
            Q1=makeQuery(id+"F28.opExtrude","SWEPT_FACE",FACE,{"disambiguationData":[OSD([sQuery(id+"F27.wireOp",EDGE,"E121")])]});
            extrude(context, id + "F31", {"entities" : qUnion([Q0]), "operationType" : NewBodyOperationType.REMOVE, "endBound" : BoundingType.UP_TO_SURFACE, "oppositeDirection" : true, "endBoundEntityFace" : qUnion([Q1]), "depth" : 25 * mm});
        }
        {
            var Q0;
            {var subQ3=sQuery(id+"F18.wireOp",EDGE,"E91");Q0=makeQuery(id+"F28.boolean.opBoolean","INTERSECT",EDGE,{"derivedFrom":[makeQuery(id+"F26.boolean.opBoolean","COPY",FACE,{"disambiguationData":[TD([makeQuery(id+"F19.opExtrude","SWEPT_FACE",FACE,{"disambiguationData":[OSD([subQ3])]})])],"derivedFrom":makeQuery(id+"F26.opExtrude","SWEPT_FACE",FACE,{"disambiguationData":[OSD([sQuery(id+"F25.wireOp",EDGE,"E117")])]})}),makeQuery(id+"F28.opExtrude","SWEPT_FACE",FACE,{"disambiguationData":[OSD([sQuery(id+"F27.wireOp",EDGE,"E123")])]})]});}
            var Q1;
            {var subQ2=sQuery(id+"F18.wireOp",EDGE,"E90");Q1=makeQuery(id+"F28.boolean.opBoolean","INTERSECT",EDGE,{"derivedFrom":[makeQuery(id+"F26.boolean.opBoolean","COPY",FACE,{"disambiguationData":[TD([makeQuery(id+"F19.opExtrude","SWEPT_FACE",FACE,{"disambiguationData":[OSD([subQ2])]})])],"derivedFrom":makeQuery(id+"F26.opExtrude","SWEPT_FACE",FACE,{"disambiguationData":[OSD([sQuery(id+"F25.wireOp",EDGE,"E117")])]})}),makeQuery(id+"F28.opExtrude","SWEPT_FACE",FACE,{"disambiguationData":[OSD([sQuery(id+"F27.wireOp",EDGE,"E121")])]})]});}
            fillet(context, id + "F32", {"entities" : qUnion([Q0, Q1]), "radius" : 6.5 * mm, "tangentPropagation" : true, "allowEdgeOverflow" : false});
        }
        {
            var Q0;
            Q0=makeQuery(id+"F28.opExtrude","SWEPT_EDGE",EDGE,{"disambiguationData":[OSD([sQuery(id+"F27.wireOp",EDGE,"E122"),sQuery(id+"F27.wireOp",EDGE,"E123")])]});
            var Q1;
            Q1=makeQuery(id+"F28.opExtrude","SWEPT_EDGE",EDGE,{"disambiguationData":[OSD([sQuery(id+"F27.wireOp",EDGE,"E121"),sQuery(id+"F27.wireOp",EDGE,"E122")])]});
            fillet(context, id + "F33", {"entities" : qUnion([Q0, Q1]), "radius" : 3 * mm, "tangentPropagation" : true, "allowEdgeOverflow" : false});
        }
        {
            var Q0;
            Q0=makeQuery(id+"F31.boolean.opBoolean","COPY",EDGE,{"derivedFrom":makeQuery(id+"F31.opExtrude","SWEPT_EDGE",EDGE,{"disambiguationData":[OSD([sQuery(id+"F25.wireOp",EDGE,"E117"),sQuery(id+"F27.wireOp",EDGE,"E123"),sQuery(id+"F30.wireOp",EDGE,"E126"),sQuery(id+"F30.wireOp",EDGE,"E128")])]})});
            var Q1;
            {var subQ0=sQuery(id+"F27.wireOp",EDGE,"E122");Q1=makeQuery(id+"F29.opChamfer","BLEND_EDGE",EDGE,{"blendedFrom":[makeQuery(id+"F28.opExtrude","CAP_EDGE",EDGE,{"disambiguationData":[OSD([subQ0])],"isStart":true}),makeQuery(id+"F28.boolean.opBoolean","MERGE",FACE,{"derivedFrom":[makeQuery(id+"F21.opExtrude","CAP_FACE",FACE,{"disambiguationData":[OSD([sQuery(id+"F20.wireOp",EDGE,"E100.0"),sQuery(id+"F20.wireOp",EDGE,"E100.1"),sQuery(id+"F20.wireOp",EDGE,"E100.2"),sQuery(id+"F20.wireOp",EDGE,"E100.3"),sQuery(id+"F20.wireOp",EDGE,"E100.4"),sQuery(id+"F20.wireOp",EDGE,"E101.0"),sQuery(id+"F20.wireOp",EDGE,"E101.1"),sQuery(id+"F20.wireOp",EDGE,"E101.2"),sQuery(id+"F20.wireOp",EDGE,"E102"),sQuery(id+"F20.wireOp",EDGE,"E103"),sQuery(id+"F20.wireOp",EDGE,"E104"),sQuery(id+"F20.wireOp",EDGE,"E105"),sQuery(id+"F20.wireOp",EDGE,"E106"),sQuery(id+"F20.wireOp",EDGE,"E110"),sQuery(id+"F20.wireOp",EDGE,"E111")])],"isStart":false}),makeQuery(id+"F28.opExtrude","CAP_FACE",FACE,{"disambiguationData":[OSD([sQuery(id+"F27.wireOp",EDGE,"E121"),subQ0,sQuery(id+"F27.wireOp",EDGE,"E123"),sQuery(id+"F27.wireOp",EDGE,"E124")])],"isStart":true})]})],"blendedInto":[makeQuery(id+"F28.boolean.opBoolean","MERGE",FACE,{"derivedFrom":[makeQuery(id+"F21.opExtrude","CAP_FACE",FACE,{"disambiguationData":[OSD([sQuery(id+"F20.wireOp",EDGE,"E100.0"),sQuery(id+"F20.wireOp",EDGE,"E100.1"),sQuery(id+"F20.wireOp",EDGE,"E100.2"),sQuery(id+"F20.wireOp",EDGE,"E100.3"),sQuery(id+"F20.wireOp",EDGE,"E100.4"),sQuery(id+"F20.wireOp",EDGE,"E101.0"),sQuery(id+"F20.wireOp",EDGE,"E101.1"),sQuery(id+"F20.wireOp",EDGE,"E101.2"),sQuery(id+"F20.wireOp",EDGE,"E102"),sQuery(id+"F20.wireOp",EDGE,"E103"),sQuery(id+"F20.wireOp",EDGE,"E104"),sQuery(id+"F20.wireOp",EDGE,"E105"),sQuery(id+"F20.wireOp",EDGE,"E106"),sQuery(id+"F20.wireOp",EDGE,"E110"),sQuery(id+"F20.wireOp",EDGE,"E111")])],"isStart":false}),makeQuery(id+"F28.opExtrude","CAP_FACE",FACE,{"disambiguationData":[OSD([sQuery(id+"F27.wireOp",EDGE,"E121"),subQ0,sQuery(id+"F27.wireOp",EDGE,"E123"),sQuery(id+"F27.wireOp",EDGE,"E124")])],"isStart":true})]})]});}
            fillet(context, id + "F34", {"entities" : qUnion([Q0, Q1]), "radius" : 1.5 * mm, "tangentPropagation" : true, "allowEdgeOverflow" : false});
        }
    });
